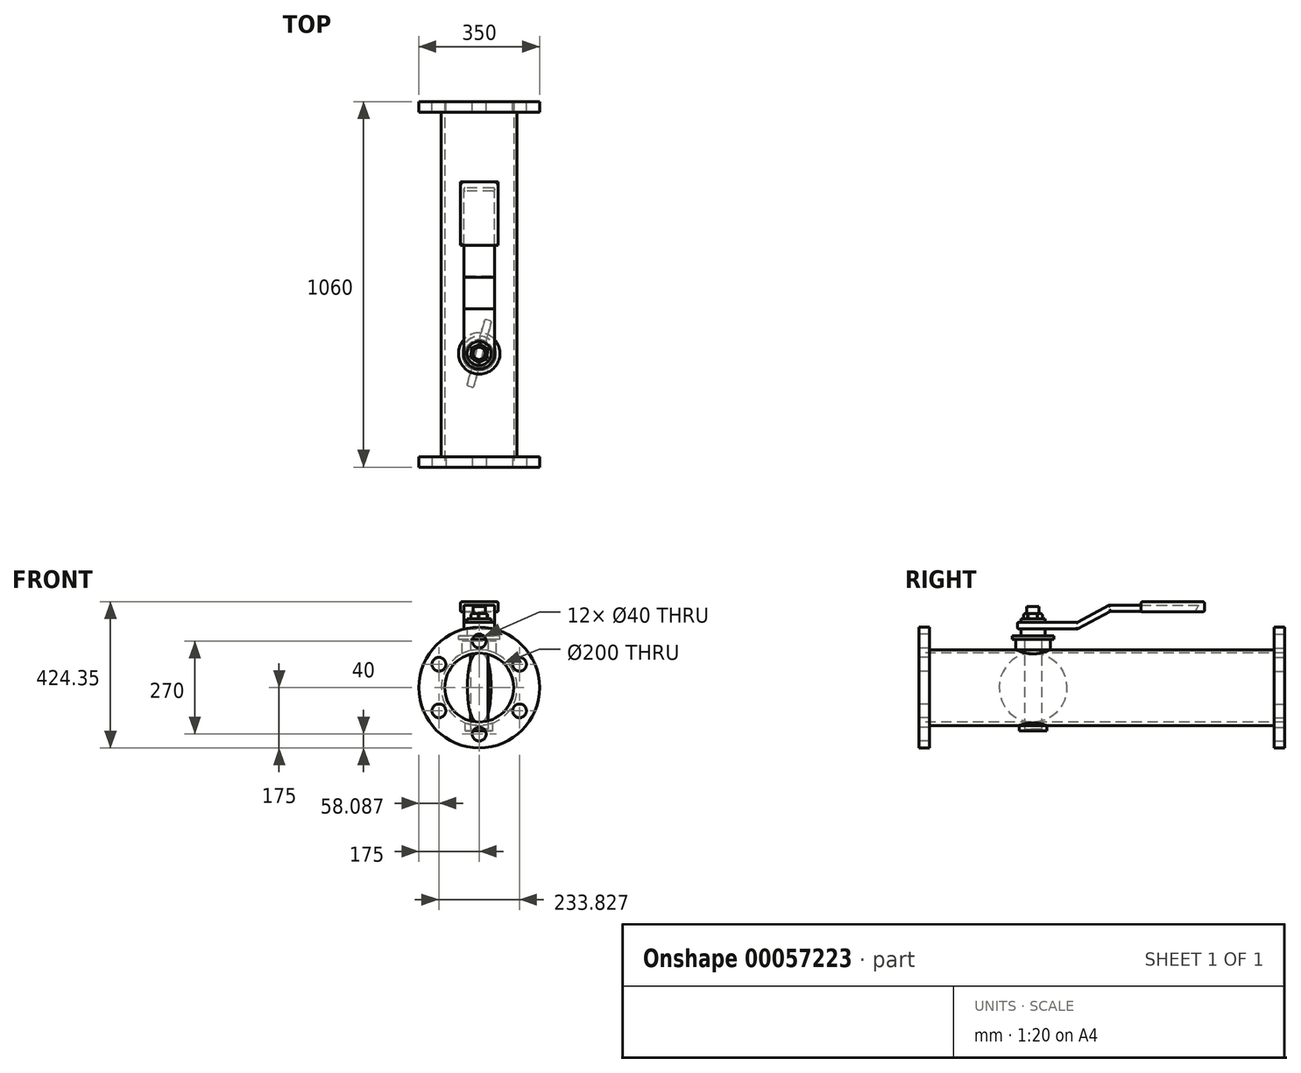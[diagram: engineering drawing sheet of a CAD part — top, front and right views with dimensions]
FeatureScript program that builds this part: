
annotation { "Feature Type Name" : "Feature", "Feature Type Description" : "" }
export const myFeature = defineFeature(function(context is Context, id is Id, definition is map)
    precondition{}
    {
        {
            var Q0;
            Q0=qCreatedBy(makeId("Front.planeOp"),FACE);
            var sketch = newSketch(context, id + "F0", { "sketchPlane" : qUnion([Q0])});
            skCircle(sketch, "E0", {"center": v(0, 0) * mm, "radius": 110 * mm});
            skSolve(sketch);
        }
        {
            var Q0;
            Q0=qSketchRegion(id+"F0",true);
            extrude(context, id + "F1", {"entities" : qUnion([Q0]), "oppositeDirection" : true, "depth" : 1000 * mm});
        }
        {
            var Q0;
            Q0=makeQuery(id+"F1.opExtrude","CAP_FACE",FACE,{"disambiguationData":[OSD([sQuery(id+"F0.wireOp",EDGE,"E0")])],"isStart":true});
            var sketch = newSketch(context, id + "F2", { "sketchPlane" : qUnion([Q0])});
            skCircle(sketch, "E1", {"center": v(0, 0) * mm, "radius": 175 * mm});
            skSolve(sketch);
        }
        {
            var Q0;
            Q0=qSketchRegion(id+"F2",true);
            extrude(context, id + "F3", {"entities" : qUnion([Q0]), "operationType" : NewBodyOperationType.ADD, "depth" : 30 * mm});
        }
        {
            var Q0;
            Q0=makeQuery(id+"F1.opExtrude","CAP_FACE",FACE,{"disambiguationData":[OSD([sQuery(id+"F0.wireOp",EDGE,"E0")])],"isStart":false});
            var sketch = newSketch(context, id + "F4", { "sketchPlane" : qUnion([Q0])});
            skCircle(sketch, "E2", {"center": v(0, 0) * mm, "radius": 175 * mm});
            skSolve(sketch);
        }
        {
            var Q0;
            Q0=qSketchRegion(id+"F4",true);
            extrude(context, id + "F5", {"entities" : qUnion([Q0]), "operationType" : NewBodyOperationType.ADD, "depth" : 30 * mm});
        }
        {
            var Q0;
            Q0=makeQuery(id+"F3.opExtrude","CAP_FACE",FACE,{"disambiguationData":[OSD([sQuery(id+"F2.wireOp",EDGE,"E1")])],"isStart":false});
            var sketch = newSketch(context, id + "F6", { "sketchPlane" : qUnion([Q0])});
            skCircle(sketch, "E3", {"center": v(0, 0) * mm, "radius": 100 * mm});
            skSolve(sketch);
        }
        {
            var Q0;
            Q0=qSketchRegion(id+"F6",true);
            var Q1;
            Q1=makeQuery(id+"F5.opExtrude","CAP_FACE",FACE,{"disambiguationData":[OSD([sQuery(id+"F4.wireOp",EDGE,"E2")])],"isStart":false});
            extrude(context, id + "F7", {"entities" : qUnion([Q0]), "operationType" : NewBodyOperationType.REMOVE, "endBound" : BoundingType.UP_TO_SURFACE, "oppositeDirection" : true, "endBoundEntityFace" : qUnion([Q1]), "depth" : 25 * mm});
        }
        {
            var Q0;
            Q0=makeQuery(id+"F3.opExtrude","CAP_FACE",FACE,{"disambiguationData":[OSD([sQuery(id+"F2.wireOp",EDGE,"E1")])],"isStart":false});
            var sketch = newSketch(context, id + "F8", { "sketchPlane" : qUnion([Q0])});
            skCircle(sketch, "E4", {"center": v(0, 135) * mm, "radius": 20 * mm});
            skCircle(sketch, "E5.1.0", {"center": v(-116.91, 67.5) * mm, "radius": 20 * mm});
            skCircle(sketch, "E5.2.0", {"center": v(-116.91, -67.5) * mm, "radius": 20 * mm});
            skCircle(sketch, "E5.3.0", {"center": v(0, -135) * mm, "radius": 20 * mm});
            skCircle(sketch, "E5.4.0", {"center": v(116.91, -67.5) * mm, "radius": 20 * mm});
            skCircle(sketch, "E5.5.0", {"center": v(116.91, 67.5) * mm, "radius": 20 * mm});
            skPoint(sketch, "E5.center", {"position": v(0, 0) * mm});
            skSolve(sketch);
        }
        {
            var Q0;
            Q0=qSketchRegion(id+"F8",true);
            var Q1;
            Q1=makeQuery(id+"F3.opExtrude","CAP_FACE",FACE,{"disambiguationData":[OSD([sQuery(id+"F2.wireOp",EDGE,"E1")])],"isStart":true});
            extrude(context, id + "F9", {"entities" : qUnion([Q0]), "operationType" : NewBodyOperationType.REMOVE, "endBound" : BoundingType.UP_TO_SURFACE, "oppositeDirection" : true, "endBoundEntityFace" : qUnion([Q1]), "depth" : 25 * mm});
        }
        {
            var Q0;
            Q0=makeQuery(id+"F5.opExtrude","CAP_FACE",FACE,{"disambiguationData":[OSD([sQuery(id+"F4.wireOp",EDGE,"E2")])],"isStart":false});
            var sketch = newSketch(context, id + "F10", { "sketchPlane" : qUnion([Q0])});
            skCircle(sketch, "E6", {"center": v(0, 135) * mm, "radius": 20 * mm});
            skCircle(sketch, "E7.1.0", {"center": v(-116.91, 67.5) * mm, "radius": 20 * mm});
            skCircle(sketch, "E7.2.0", {"center": v(-116.91, -67.5) * mm, "radius": 20 * mm});
            skCircle(sketch, "E7.3.0", {"center": v(0, -135) * mm, "radius": 20 * mm});
            skCircle(sketch, "E7.4.0", {"center": v(116.91, -67.5) * mm, "radius": 20 * mm});
            skCircle(sketch, "E7.5.0", {"center": v(116.91, 67.5) * mm, "radius": 20 * mm});
            skPoint(sketch, "E7.center", {"position": v(0, 0) * mm});
            skSolve(sketch);
        }
        {
            var Q0;
            Q0=qSketchRegion(id+"F10",true);
            var Q1;
            Q1=makeQuery(id+"F5.opExtrude","CAP_FACE",FACE,{"disambiguationData":[OSD([sQuery(id+"F4.wireOp",EDGE,"E2")])],"isStart":true});
            extrude(context, id + "F11", {"entities" : qUnion([Q0]), "operationType" : NewBodyOperationType.REMOVE, "endBound" : BoundingType.UP_TO_SURFACE, "oppositeDirection" : true, "endBoundEntityFace" : qUnion([Q1]), "depth" : 25 * mm});
        }
        {
            var Q0;
            Q0=qCreatedBy(makeId("Front.planeOp"),FACE);
            cPlane(context, id + "F12", {"entities" : qUnion([Q0]), "cplaneType" : CPlaneType.OFFSET, "offset" : 300 * mm, "oppositeDirection" : true, "width" : 150 * mm, "height" : 150 * mm});
        }
        {
            var Q0;
            Q0=qCreatedBy(id+"F12.planeOp",FACE);
            var sketch = newSketch(context, id + "F13", { "sketchPlane" : qUnion([Q0])});
            skCircle(sketch, "E8", {"center": v(0, 0) * mm, "radius": 100 * mm});
            skSolve(sketch);
        }
        {
            var Q0;
            Q0=qSketchRegion(id+"F13",true);
            extrude(context, id + "F14", {"entities" : qUnion([Q0]), "depth" : 10 * mm, "hasSecondDirection" : true, "secondDirectionOppositeDirection" : true, "secondDirectionDepth" : 10 * mm});
        }
        {
            var Q0;
            Q0=makeQuery(id+"F14.opExtrude","CAP_EDGE",EDGE,{"disambiguationData":[OSD([sQuery(id+"F13.wireOp",EDGE,"E8")])],"isStart":false});
            var Q1;
            Q1=makeQuery(id+"F14.opExtrude","CAP_EDGE",EDGE,{"disambiguationData":[OSD([sQuery(id+"F13.wireOp",EDGE,"E8")])],"isStart":true});
            fillet(context, id + "F15", {"entities" : qUnion([Q0, Q1]), "radius" : 5 * mm, "tangentPropagation" : true, "allowEdgeOverflow" : false});
        }
        {
            var Q0;
            Q0=qCreatedBy(makeId("Top.planeOp"),FACE);
            var sketch = newSketch(context, id + "F16", { "sketchPlane" : qUnion([Q0])});
            skCircle(sketch, "E9", {"center": v(0, 300) * mm, "radius": 25 * mm});
            skSolve(sketch);
        }
        {
            var Q0;
            Q0=qSketchRegion(id+"F16",true);
            extrude(context, id + "F17", {"entities" : qUnion([Q0]), "depth" : 150 * mm, "hasSecondDirection" : true, "secondDirectionOppositeDirection" : true, "secondDirectionDepth" : 120 * mm});
        }
        {
            var Q0;
            Q0=makeQuery(id+"F17.opExtrude","CAP_FACE",FACE,{"disambiguationData":[OSD([sQuery(id+"F16.wireOp",EDGE,"E9")])],"isStart":true});
            var sketch = newSketch(context, id + "F18", { "sketchPlane" : qUnion([Q0])});
            skCircle(sketch, "E10", {"center": v(0, -300) * mm, "radius": 40 * mm});
            skSolve(sketch);
        }
        {
            var Q0;
            Q0=qSketchRegion(id+"F18",true);
            var Q1;
            Q1=makeQuery(id+"F1.opExtrude","SWEPT_FACE",FACE,{"disambiguationData":[OSD([sQuery(id+"F0.wireOp",EDGE,"E0")])]});
            extrude(context, id + "F19", {"entities" : qUnion([Q0]), "depth" : 5 * mm, "hasSecondDirection" : true, "secondDirectionBound" : SecondDirectionBoundingType.UP_TO_SURFACE, "secondDirectionOppositeDirection" : true, "secondDirectionBoundEntityFace" : qUnion([Q1]), "secondDirectionDepth" : 25 * mm});
        }
        {
            var Q0;
            Q0=makeQuery(id+"F17.opExtrude","CAP_FACE",FACE,{"disambiguationData":[OSD([sQuery(id+"F16.wireOp",EDGE,"E9")])],"isStart":false});
            var sketch = newSketch(context, id + "F20", { "sketchPlane" : qUnion([Q0])});
            skCircle(sketch, "E11", {"center": v(0, 300) * mm, "radius": 60 * mm});
            skSolve(sketch);
        }
        {
            var Q0;
            Q0=qSketchRegion(id+"F20",true);
            extrude(context, id + "F21", {"entities" : qUnion([Q0]), "operationType" : NewBodyOperationType.ADD, "oppositeDirection" : true, "depth" : 10 * mm});
        }
        {
            var Q0;
            Q0=makeQuery(id+"F21.opExtrude","CAP_FACE",FACE,{"disambiguationData":[OSD([sQuery(id+"F20.wireOp",EDGE,"E11")])],"isStart":false});
            var sketch = newSketch(context, id + "F22", { "sketchPlane" : qUnion([Q0])});
            skCircle(sketch, "E12", {"center": v(0, -300) * mm, "radius": 50 * mm});
            skSolve(sketch);
        }
        {
            var Q0;
            Q0=qSketchRegion(id+"F22",true);
            var Q1;
            Q1=makeQuery(id+"F1.opExtrude","SWEPT_FACE",FACE,{"disambiguationData":[OSD([sQuery(id+"F0.wireOp",EDGE,"E0")])]});
            extrude(context, id + "F23", {"entities" : qUnion([Q0]), "endBound" : BoundingType.UP_TO_SURFACE, "endBoundEntityFace" : qUnion([Q1]), "depth" : 25 * mm});
        }
        {
            var Q0;
            Q0=makeQuery(id+"F21.boolean.opBoolean","MERGE",FACE,{"derivedFrom":[makeQuery(id+"F17.opExtrude","CAP_FACE",FACE,{"disambiguationData":[OSD([sQuery(id+"F16.wireOp",EDGE,"E9")])],"isStart":false}),makeQuery(id+"F21.opExtrude","CAP_FACE",FACE,{"disambiguationData":[OSD([sQuery(id+"F20.wireOp",EDGE,"E11")])],"isStart":true})]});
            var sketch = newSketch(context, id + "F24", { "sketchPlane" : qUnion([Q0])});
            skCircle(sketch, "E13", {"center": v(0, 300) * mm, "radius": 35 * mm});
            skSolve(sketch);
        }
        {
            var Q0;
            Q0=qSketchRegion(id+"F24",true);
            extrude(context, id + "F25", {"entities" : qUnion([Q0]), "operationType" : NewBodyOperationType.ADD, "depth" : 50 * mm});
        }
        {
            var Q0;
            Q0=makeQuery(id+"F25.opExtrude","CAP_FACE",FACE,{"disambiguationData":[OSD([sQuery(id+"F24.wireOp",EDGE,"E13")])],"isStart":false});
            var sketch = newSketch(context, id + "F26", { "sketchPlane" : qUnion([Q0])});
            skCircle(sketch, "E14", {"center": v(0, 300) * mm, "radius": 17.5 * mm});
            skSolve(sketch);
        }
        {
            var Q0;
            Q0=qSketchRegion(id+"F26",true);
            extrude(context, id + "F27", {"entities" : qUnion([Q0]), "operationType" : NewBodyOperationType.ADD, "depth" : 35 * mm});
        }
        {
            var Q0;
            Q0=makeQuery(id+"F25.opExtrude","CAP_FACE",FACE,{"disambiguationData":[OSD([sQuery(id+"F24.wireOp",EDGE,"E13")])],"isStart":false});
            var sketch = newSketch(context, id + "F28", { "sketchPlane" : qUnion([Q0])});
            skCircle(sketch, "E15.cCircle", {"center": v(0, 300) * mm, "radius": 23.41 * mm, "construction": true});
            skLineSegment(sketch, "E15.0", {"start": v(-22.44, 315.08) * mm, "end": v(1.84, 326.97) * mm});
            skLineSegment(sketch, "E15.1", {"start": v(1.84, 326.97) * mm, "end": v(24.28, 311.9) * mm});
            skLineSegment(sketch, "E15.2", {"start": v(24.28, 311.9) * mm, "end": v(22.44, 284.92) * mm});
            skLineSegment(sketch, "E15.3", {"start": v(22.44, 284.92) * mm, "end": v(-1.84, 273.03) * mm});
            skLineSegment(sketch, "E15.4", {"start": v(-1.84, 273.03) * mm, "end": v(-24.28, 288.1) * mm});
            skLineSegment(sketch, "E15.5", {"start": v(-24.28, 288.1) * mm, "end": v(-22.44, 315.08) * mm});
            skPoint(sketch, "E15.0.midPoint", {"position": v(-10.3, 321.02) * mm});
            skSolve(sketch);
        }
        {
            var Q0;
            Q0=qSketchRegion(id+"F28",true);
            extrude(context, id + "F29", {"entities" : qUnion([Q0]), "operationType" : NewBodyOperationType.ADD, "depth" : 15 * mm});
        }
        {
            var Q0;
            Q0=makeQuery(id+"F29.opExtrude","CAP_EDGE",EDGE,{"disambiguationData":[OSD([sQuery(id+"F28.wireOp",EDGE,"E15.3")])],"isStart":false});
            var Q1;
            Q1=makeQuery(id+"F29.opExtrude","CAP_EDGE",EDGE,{"disambiguationData":[OSD([sQuery(id+"F28.wireOp",EDGE,"E15.2")])],"isStart":false});
            var Q2;
            Q2=makeQuery(id+"F29.opExtrude","CAP_EDGE",EDGE,{"disambiguationData":[OSD([sQuery(id+"F28.wireOp",EDGE,"E15.1")])],"isStart":false});
            var Q3;
            Q3=makeQuery(id+"F29.opExtrude","CAP_EDGE",EDGE,{"disambiguationData":[OSD([sQuery(id+"F28.wireOp",EDGE,"E15.0")])],"isStart":false});
            var Q4;
            Q4=makeQuery(id+"F29.opExtrude","CAP_EDGE",EDGE,{"disambiguationData":[OSD([sQuery(id+"F28.wireOp",EDGE,"E15.5")])],"isStart":false});
            var Q5;
            Q5=makeQuery(id+"F29.opExtrude","CAP_EDGE",EDGE,{"disambiguationData":[OSD([sQuery(id+"F28.wireOp",EDGE,"E15.4")])],"isStart":false});
            fillet(context, id + "F30", {"entities" : qUnion([Q0, Q1, Q2, Q3, Q4, Q5]), "radius" : 5 * mm, "tangentPropagation" : true, "allowEdgeOverflow" : false});
        }
        {
            var Q0;
            Q0=makeQuery(id+"F21.boolean.opBoolean","MERGE",FACE,{"derivedFrom":[makeQuery(id+"F17.opExtrude","CAP_FACE",FACE,{"disambiguationData":[OSD([sQuery(id+"F16.wireOp",EDGE,"E9")])],"isStart":false}),makeQuery(id+"F21.opExtrude","CAP_FACE",FACE,{"disambiguationData":[OSD([sQuery(id+"F20.wireOp",EDGE,"E11")])],"isStart":true})]});
            cPlane(context, id + "F31", {"entities" : qUnion([Q0]), "cplaneType" : CPlaneType.OFFSET, "offset" : 20 * mm, "width" : 150 * mm, "height" : 150 * mm});
        }
        {
            var Q0;
            Q0=qCreatedBy(id+"F31.planeOp",FACE);
            var sketch = newSketch(context, id + "F32", { "sketchPlane" : qUnion([Q0])});
            skCircle(sketch, "E16", {"center": v(0, 300) * mm, "radius": 45 * mm});
            skLineSegment(sketch, "E17", {"start": v(45, 300) * mm, "end": v(45, 428.94) * mm});
            skLineSegment(sketch, "E18", {"start": v(45, 428.94) * mm, "end": v(-45, 428.94) * mm});
            skLineSegment(sketch, "E19", {"start": v(-45, 428.94) * mm, "end": v(-45, 300) * mm});
            skSolve(sketch);
        }
        {
            var Q0;
            Q0=qSketchRegion(id+"F32",true);
            extrude(context, id + "F33", {"entities" : qUnion([Q0]), "operationType" : NewBodyOperationType.ADD, "depth" : 20 * mm});
        }
        {
            var Q0;
            Q0=makeQuery(id+"F33.opExtrude","SWEPT_FACE",FACE,{"disambiguationData":[OSD([sQuery(id+"F32.wireOp",EDGE,"E17")])]});
            var sketch = newSketch(context, id + "F34", { "sketchPlane" : qUnion([Q0])});
            skLineSegment(sketch, "E20", {"start": v(428.94, 190) * mm, "end": v(520.25, 239.35) * mm});
            skLineSegment(sketch, "E21", {"start": v(520.25, 239.35) * mm, "end": v(779.97, 239.35) * mm});
            skSolve(sketch);
        }
        {
            var Q0;
            Q0=makeQuery(id+"F33.opExtrude","SWEPT_FACE",FACE,{"disambiguationData":[OSD([sQuery(id+"F32.wireOp",EDGE,"E18")])]});
            var Q1;
            Q1=sQuery(id+"F34.wireOp",EDGE,"E20");
            var Q2;
            Q2=sQuery(id+"F34.wireOp",EDGE,"E21");
            sweep(context, id + "F35", {"operationType" : NewBodyOperationType.ADD, "profiles" : qUnion([Q0]), "path" : qUnion([Q1, Q2])});
        }
        {
            var Q0;
            Q0=makeQuery(id+"F33.opExtrude","CAP_EDGE",EDGE,{"disambiguationData":[OSD([sQuery(id+"F32.wireOp",EDGE,"E17")])],"isStart":false});
            var Q1;
            Q1=makeQuery(id+"F33.opExtrude","CAP_EDGE",EDGE,{"disambiguationData":[OSD([sQuery(id+"F32.wireOp",EDGE,"E19")])],"isStart":false});
            var Q2;
            {var subQ0=sQuery(id+"F34.wireOp",EDGE,"E20");var subQ1=sQuery(id+"F32.wireOp",EDGE,"E18");var subQ2=sQuery(id+"F32.wireOp",EDGE,"E17");Q2=makeQuery(id+"F35.opSweep","SWEPT_EDGE",EDGE,{"disambiguationData":[OSD([subQ2,subQ1,subQ0]),TDD([makeQuery(id+"F33.opExtrude","CAP_VERTEX",VERTEX,{"disambiguationData":[OSD([subQ2,subQ1])],"isStart":false}),subQ0])]});}
            var Q3;
            {var subQ0=sQuery(id+"F34.wireOp",EDGE,"E21");var subQ1=sQuery(id+"F32.wireOp",EDGE,"E18");var subQ2=sQuery(id+"F32.wireOp",EDGE,"E17");Q3=makeQuery(id+"F35.opSweep","SWEPT_EDGE",EDGE,{"disambiguationData":[OSD([subQ2,subQ1,subQ0]),TDD([makeQuery(id+"F33.opExtrude","CAP_VERTEX",VERTEX,{"disambiguationData":[OSD([subQ2,subQ1])],"isStart":false}),subQ0])]});}
            var Q4;
            {var subQ0=sQuery(id+"F34.wireOp",EDGE,"E21");var subQ1=sQuery(id+"F32.wireOp",EDGE,"E18");var subQ2=sQuery(id+"F32.wireOp",EDGE,"E17");Q4=makeQuery(id+"F35.opSweep","SWEPT_EDGE",EDGE,{"disambiguationData":[OSD([subQ2,subQ1,subQ0]),TDD([makeQuery(id+"F33.opExtrude","CAP_VERTEX",VERTEX,{"disambiguationData":[OSD([subQ2,subQ1])],"isStart":true}),subQ0])]});}
            var Q5;
            {var subQ0=sQuery(id+"F34.wireOp",EDGE,"E20");var subQ1=sQuery(id+"F32.wireOp",EDGE,"E18");var subQ2=sQuery(id+"F32.wireOp",EDGE,"E17");Q5=makeQuery(id+"F35.opSweep","SWEPT_EDGE",EDGE,{"disambiguationData":[OSD([subQ2,subQ1,subQ0]),TDD([makeQuery(id+"F33.opExtrude","CAP_VERTEX",VERTEX,{"disambiguationData":[OSD([subQ2,subQ1])],"isStart":true}),subQ0])]});}
            var Q6;
            Q6=makeQuery(id+"F33.opExtrude","CAP_EDGE",EDGE,{"disambiguationData":[OSD([sQuery(id+"F32.wireOp",EDGE,"E17")])],"isStart":true});
            var Q7;
            {var subQ0=sQuery(id+"F34.wireOp",EDGE,"E20");var subQ1=sQuery(id+"F32.wireOp",EDGE,"E19");var subQ2=sQuery(id+"F32.wireOp",EDGE,"E18");Q7=makeQuery(id+"F35.opSweep","SWEPT_EDGE",EDGE,{"disambiguationData":[OSD([subQ2,subQ1,subQ0]),TDD([makeQuery(id+"F33.opExtrude","CAP_VERTEX",VERTEX,{"disambiguationData":[OSD([subQ2,subQ1])],"isStart":false}),subQ0])]});}
            var Q8;
            {var subQ0=sQuery(id+"F34.wireOp",EDGE,"E21");var subQ1=sQuery(id+"F32.wireOp",EDGE,"E19");var subQ2=sQuery(id+"F32.wireOp",EDGE,"E18");Q8=makeQuery(id+"F35.opSweep","SWEPT_EDGE",EDGE,{"disambiguationData":[OSD([subQ2,subQ1,subQ0]),TDD([makeQuery(id+"F33.opExtrude","CAP_VERTEX",VERTEX,{"disambiguationData":[OSD([subQ2,subQ1])],"isStart":false}),subQ0])]});}
            var Q9;
            {var subQ0=sQuery(id+"F34.wireOp",EDGE,"E21");var subQ1=sQuery(id+"F32.wireOp",EDGE,"E19");var subQ2=sQuery(id+"F32.wireOp",EDGE,"E18");Q9=makeQuery(id+"F35.opSweep","SWEPT_EDGE",EDGE,{"disambiguationData":[OSD([subQ2,subQ1,subQ0]),TDD([makeQuery(id+"F33.opExtrude","CAP_VERTEX",VERTEX,{"disambiguationData":[OSD([subQ2,subQ1])],"isStart":true}),subQ0])]});}
            var Q10;
            {var subQ0=sQuery(id+"F34.wireOp",EDGE,"E20");var subQ1=sQuery(id+"F32.wireOp",EDGE,"E19");var subQ2=sQuery(id+"F32.wireOp",EDGE,"E18");Q10=makeQuery(id+"F35.opSweep","SWEPT_EDGE",EDGE,{"disambiguationData":[OSD([subQ2,subQ1,subQ0]),TDD([makeQuery(id+"F33.opExtrude","CAP_VERTEX",VERTEX,{"disambiguationData":[OSD([subQ2,subQ1])],"isStart":true}),subQ0])]});}
            fillet(context, id + "F36", {"entities" : qUnion([Q0, Q1, Q2, Q3, Q4, Q5, Q6, Q7, Q8, Q9, Q10]), "radius" : 5 * mm, "tangentPropagation" : true, "allowEdgeOverflow" : false});
        }
        {
            var Q0;
            {var subQ0=sQuery(id+"F34.wireOp",EDGE,"E21");var subQ1=sQuery(id+"F32.wireOp",EDGE,"E18");Q0=makeQuery(id+"F35.opSweep","SWEPT_FACE",FACE,{"disambiguationData":[OSD([subQ1,subQ0]),TDD([makeQuery(id+"F33.opExtrude","CAP_EDGE",EDGE,{"disambiguationData":[OSD([subQ1])],"isStart":false}),subQ0])]});}
            var sketch = newSketch(context, id + "F37", { "sketchPlane" : qUnion([Q0])});
            skLineSegment(sketch, "E22.bottom", {"start": v(-54.54, 613.19) * mm, "end": v(54.99, 613.19) * mm});
            skLineSegment(sketch, "E22.top", {"start": v(-54.54, 797.38) * mm, "end": v(54.99, 797.38) * mm});
            skLineSegment(sketch, "E22.left", {"start": v(-54.54, 613.19) * mm, "end": v(-54.54, 797.38) * mm});
            skLineSegment(sketch, "E22.right", {"start": v(54.99, 613.19) * mm, "end": v(54.99, 797.38) * mm});
            skSolve(sketch);
        }
        {
            var Q0;
            Q0=qSketchRegion(id+"F37",true);
            extrude(context, id + "F38", {"entities" : qUnion([Q0]), "depth" : 10 * mm, "hasSecondDirection" : true, "secondDirectionOppositeDirection" : true, "secondDirectionDepth" : 20 * mm});
        }
        {
            var Q0;
            Q0=makeQuery(id+"F38.opExtrude","CAP_EDGE",EDGE,{"disambiguationData":[OSD([sQuery(id+"F37.wireOp",EDGE,"E22.right")])],"isStart":false});
            var Q1;
            Q1=makeQuery(id+"F38.opExtrude","CAP_EDGE",EDGE,{"disambiguationData":[OSD([sQuery(id+"F37.wireOp",EDGE,"E22.bottom")])],"isStart":false});
            var Q2;
            Q2=makeQuery(id+"F38.opExtrude","CAP_EDGE",EDGE,{"disambiguationData":[OSD([sQuery(id+"F37.wireOp",EDGE,"E22.left")])],"isStart":false});
            var Q3;
            Q3=makeQuery(id+"F38.opExtrude","CAP_EDGE",EDGE,{"disambiguationData":[OSD([sQuery(id+"F37.wireOp",EDGE,"E22.top")])],"isStart":false});
            var Q4;
            Q4=makeQuery(id+"F38.opExtrude","CAP_EDGE",EDGE,{"disambiguationData":[OSD([sQuery(id+"F37.wireOp",EDGE,"E22.right")])],"isStart":true});
            var Q5;
            Q5=makeQuery(id+"F38.opExtrude","CAP_EDGE",EDGE,{"disambiguationData":[OSD([sQuery(id+"F37.wireOp",EDGE,"E22.bottom")])],"isStart":true});
            var Q6;
            Q6=makeQuery(id+"F38.opExtrude","CAP_EDGE",EDGE,{"disambiguationData":[OSD([sQuery(id+"F37.wireOp",EDGE,"E22.left")])],"isStart":true});
            var Q7;
            Q7=makeQuery(id+"F38.opExtrude","CAP_EDGE",EDGE,{"disambiguationData":[OSD([sQuery(id+"F37.wireOp",EDGE,"E22.top")])],"isStart":true});
            fillet(context, id + "F39", {"entities" : qUnion([Q0, Q1, Q2, Q3, Q4, Q5, Q6, Q7]), "radius" : 5 * mm, "tangentPropagation" : true, "allowEdgeOverflow" : false});
        }
        {
            var Q0;
            Q0=qCreatedBy(makeId("Right.planeOp"),FACE);
            var sketch = newSketch(context, id + "F40", { "sketchPlane" : qUnion([Q0])});
            skLineSegment(sketch, "E23", {"start": v(300, 235) * mm, "end": v(300, -134.3) * mm, "construction": true});
            skSolve(sketch);
        }
        {
            var Q0;
            Q0=makeQuery(id+"F14.opExtrude","SWEPT_BODY",BODY,{"disambiguationData":[OSD([sQuery(id+"F13.wireOp",EDGE,"E8")])]});
            var Q1;
            Q1=sQuery(id+"F40.wireOp",EDGE,"E23");
            transform(context, id + "F41", {"entities" : qUnion([Q0]), "transformType" : TransformType.ROTATION, "transformAxis" : qUnion([Q1]), "angle" : 75 * degree, "oppositeDirection" : true, "makeCopy" : false});
        }
    });
